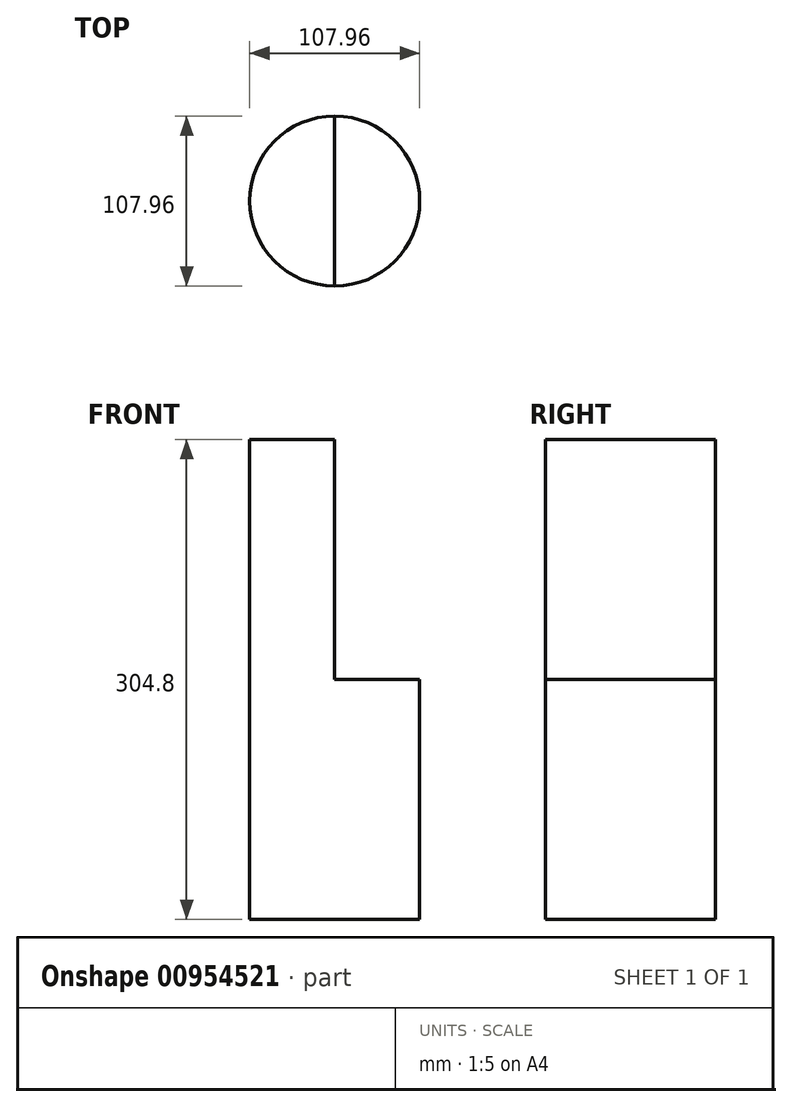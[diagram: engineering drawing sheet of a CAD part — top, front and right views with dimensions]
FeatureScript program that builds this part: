
annotation { "Feature Type Name" : "Feature", "Feature Type Description" : "" }
export const myFeature = defineFeature(function(context is Context, id is Id, definition is map)
    precondition{}
    {
        {
            var Q0;
            Q0=qCreatedBy(makeId("Top.planeOp"),FACE);
            var sketch = newSketch(context, id + "F0", { "sketchPlane" : qUnion([Q0])});
            skCircle(sketch, "E0", {"center": v(0, 0) * mm, "radius": 53.98 * mm});
            skSolve(sketch);
        }
        {
            var Q0;
            Q0=makeQuery(id+"F0.imprint","IMPRINT",FACE,{"disambiguationData":[TD([[makeQuery(id+"F0.imprint","IMPRINT",EDGE,{"derivedFrom":sQuery(id+"F0.wireOp",EDGE,"E0")}),1.0]])]});
            extrude(context, id + "F1", {"entities" : qUnion([Q0]), "endBound" : BoundingType.SYMMETRIC, "depth" : 304.8 * mm, "offsetDistance" : 25.4 * mm});
        }
        {
            var Q0;
            Q0=makeQuery(id+"F1.opExtrude","CAP_FACE",FACE,{"disambiguationData":[OSD([sQuery(id+"F0.wireOp",EDGE,"E0")])],"isStart":false});
            var sketch = newSketch(context, id + "F2", { "sketchPlane" : qUnion([Q0])});
            skArc(sketch, "E1", {"start": v(0, -53.97) * mm, "mid": v(53.97, 0) * mm, "end": v(0, 53.97) * mm});
            skLineSegment(sketch, "E2", {"start": v(0, 53.98) * mm, "end": v(0, -53.98) * mm});
            skSolve(sketch);
        }
        {
            var Q0;
            Q0=makeQuery(id+"F2.imprint","IMPRINT",FACE,{"disambiguationData":[TD([[makeQuery(id+"F2.imprint","IMPRINT",EDGE,{"derivedFrom":sQuery(id+"F2.wireOp",EDGE,"E1")}),1.0]])]});
            extrude(context, id + "F3", {"entities" : qUnion([Q0]), "operationType" : NewBodyOperationType.REMOVE, "oppositeDirection" : true, "depth" : 152.4 * mm, "offsetDistance" : 25.4 * mm});
        }
    });
